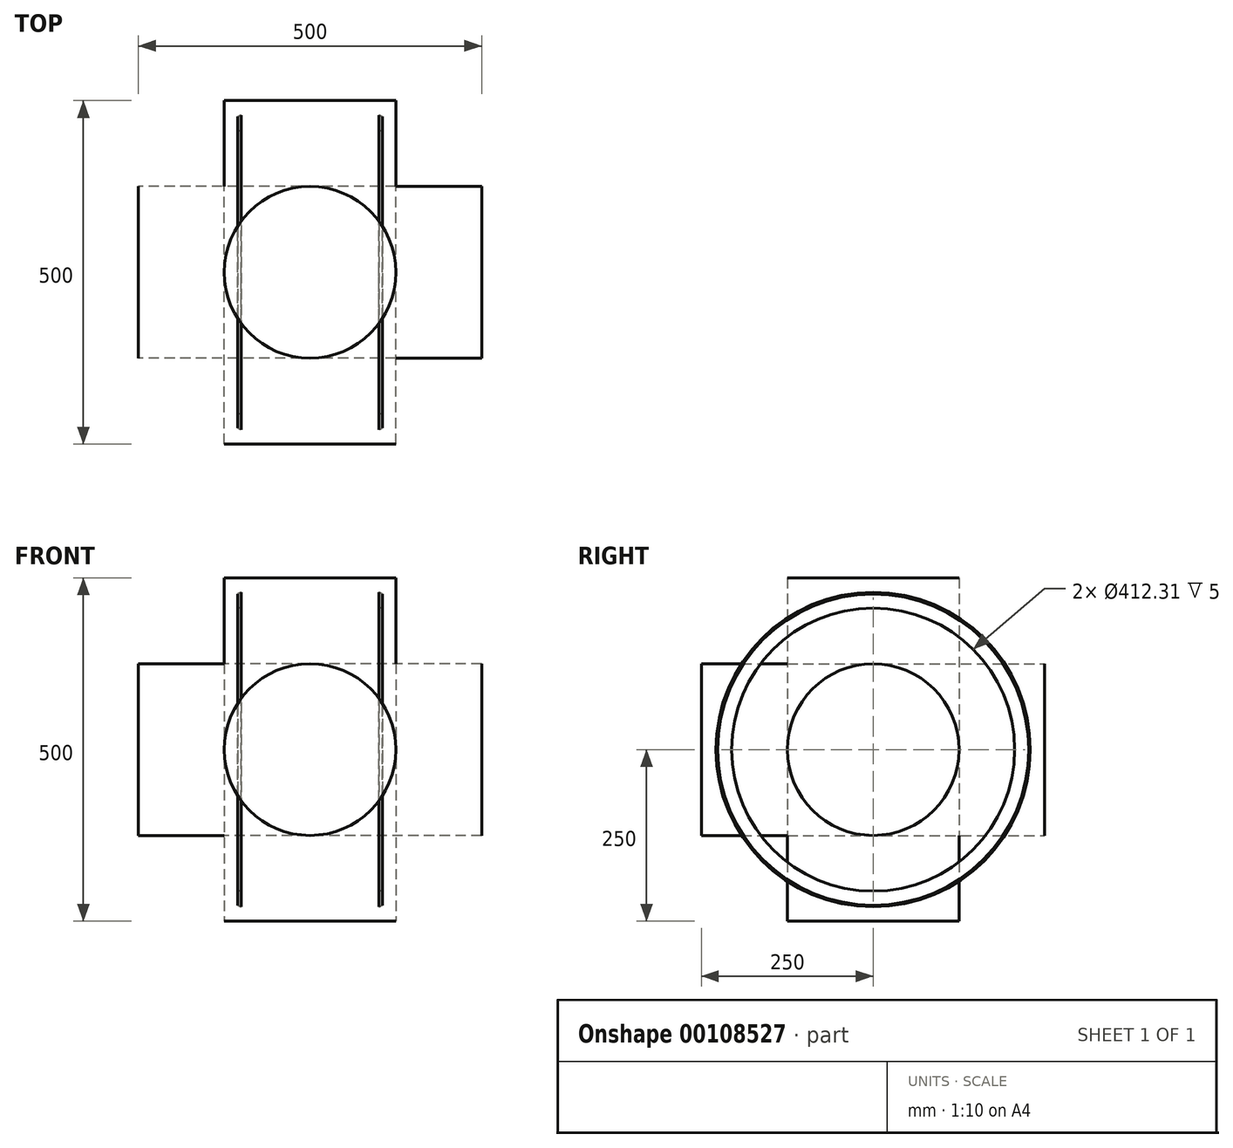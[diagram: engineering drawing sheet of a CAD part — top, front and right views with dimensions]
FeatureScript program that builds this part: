
annotation { "Feature Type Name" : "Feature", "Feature Type Description" : "" }
export const myFeature = defineFeature(function(context is Context, id is Id, definition is map)
    precondition{}
    {
        {
            var Q0;
            Q0=qCreatedBy(makeId("Top.planeOp"),FACE);
            var sketch = newSketch(context, id + "F0", { "sketchPlane" : qUnion([Q0])});
            skArc(sketch, "E0", {"start": v(-95, 225.83) * mm, "mid": v(0, 245) * mm, "end": v(95, 225.83) * mm});
            skArc(sketch, "E1", {"start": v(-100, 229.13) * mm, "mid": v(0, 250) * mm, "end": v(100, 229.13) * mm});
            skPoint(sketch, "E2", {"position": v(0, 250) * mm});
            skLineSegment(sketch, "E3", {"start": v(-100, 229.13) * mm, "end": v(-100, 206.15) * mm});
            skLineSegment(sketch, "E4", {"start": v(-100, 206.15) * mm, "end": v(-95, 206.15) * mm});
            skLineSegment(sketch, "E5", {"start": v(100, 229.13) * mm, "end": v(100, 206.15) * mm});
            skLineSegment(sketch, "E6", {"start": v(100, 206.15) * mm, "end": v(95, 206.15) * mm});
            skLineSegment(sketch, "E7", {"start": v(-49.24, 240) * mm, "end": v(49.24, 240) * mm});
            skPoint(sketch, "E8", {"position": v(0, 240) * mm});
            skLineSegment(sketch, "E9", {"start": v(-95, 0) * mm, "end": v(95, 0) * mm, "construction": true});
            skLineSegment(sketch, "E10", {"start": v(-95, 206.15) * mm, "end": v(-95, 0) * mm, "construction": true});
            skLineSegment(sketch, "E11", {"start": v(95, 206.15) * mm, "end": v(95, 225.83) * mm});
            skLineSegment(sketch, "E12", {"start": v(-95, 206.15) * mm, "end": v(-95, 225.83) * mm});
            skLineSegment(sketch, "E13", {"start": v(95, 0) * mm, "end": v(95, 206.15) * mm, "construction": true});
            skLineSegment(sketch, "E14.bottom", {"start": v(10, 245) * mm, "end": v(-10, 245) * mm});
            skLineSegment(sketch, "E14.top", {"start": v(10, 240) * mm, "end": v(-10, 240) * mm});
            skLineSegment(sketch, "E14.left", {"start": v(10, 245) * mm, "end": v(10, 240) * mm});
            skLineSegment(sketch, "E14.right", {"start": v(-10, 245) * mm, "end": v(-10, 240) * mm});
            skPoint(sketch, "E14.middle", {"position": v(0, 242.5) * mm});
            skLineSegment(sketch, "E15", {"start": v(95, 225) * mm, "end": v(85, 225) * mm});
            skLineSegment(sketch, "E16", {"start": v(85, 225) * mm, "end": v(85, 229.78) * mm});
            skLineSegment(sketch, "E17", {"start": v(-95, 225) * mm, "end": v(-85, 225) * mm});
            skLineSegment(sketch, "E18", {"start": v(-85, 225) * mm, "end": v(-85, 229.78) * mm});
            skLineSegment(sketch, "E19", {"start": v(-85, 225) * mm, "end": v(85, 225) * mm, "construction": true});
            skPoint(sketch, "E20.positionSnap0", {"position": v(0, 225) * mm});
            skLineSegment(sketch, "E21", {"start": v(-95, 225.83) * mm, "end": v(95, 225.83) * mm, "construction": true});
            skPoint(sketch, "E22", {"position": v(0, 225.83) * mm});
            skLineSegment(sketch, "E23", {"start": v(85, 225) * mm, "end": v(85, 220) * mm});
            skLineSegment(sketch, "E24", {"start": v(85, 220) * mm, "end": v(87.5, 220) * mm});
            skLineSegment(sketch, "E25", {"start": v(87.5, 220) * mm, "end": v(87.5, 225) * mm});
            skLineSegment(sketch, "E26", {"start": v(-85, 225) * mm, "end": v(-85, 220) * mm});
            skLineSegment(sketch, "E27", {"start": v(-85, 220) * mm, "end": v(-87.5, 220) * mm});
            skLineSegment(sketch, "E28", {"start": v(-87.5, 220) * mm, "end": v(-87.5, 225) * mm});
            skLineSegment(sketch, "E29", {"start": v(100.5, 0) * mm, "end": v(250, 0) * mm, "construction": true});
            skLineSegment(sketch, "E30", {"start": v(-100.5, 0) * mm, "end": v(-250, 0) * mm, "construction": true});
            skArc(sketch, "E31", {"start": v(100.5, 228.9) * mm, "mid": v(209.31, 136.7) * mm, "end": v(250, 0) * mm});
            skArc(sketch, "E32", {"start": v(-100.5, 228.9) * mm, "mid": v(-209.31, 136.7) * mm, "end": v(-250, 0) * mm});
            skArc(sketch, "E33", {"start": v(105.5, 215.57) * mm, "mid": v(203.62, 127.04) * mm, "end": v(240, 0) * mm});
            skArc(sketch, "E34", {"start": v(-105.5, 215.57) * mm, "mid": v(-203.62, 127.04) * mm, "end": v(-240, 0) * mm});
            skLineSegment(sketch, "E35", {"start": v(-250, 0) * mm, "end": v(-240, 0) * mm});
            skLineSegment(sketch, "E36", {"start": v(240, 0) * mm, "end": v(250, 0) * mm});
            skLineSegment(sketch, "E37", {"start": v(100.5, 206.15) * mm, "end": v(105.5, 206.15) * mm});
            skLineSegment(sketch, "E38", {"start": v(105.5, 206.15) * mm, "end": v(105.5, 215.57) * mm});
            skLineSegment(sketch, "E39", {"start": v(100.5, 228.9) * mm, "end": v(100.5, 206.15) * mm});
            skLineSegment(sketch, "E40", {"start": v(-100.5, 206.15) * mm, "end": v(-105.5, 206.15) * mm});
            skLineSegment(sketch, "E41", {"start": v(-105.5, 206.15) * mm, "end": v(-105.5, 215.57) * mm});
            skLineSegment(sketch, "E42", {"start": v(-100.5, 228.9) * mm, "end": v(-100.5, 206.15) * mm});
            skLineSegment(sketch, "E43", {"start": v(105.5, 215.57) * mm, "end": v(105.5, 226.65) * mm});
            skLineSegment(sketch, "E44", {"start": v(-105.5, 215.57) * mm, "end": v(-105.5, 226.65) * mm});
            skSolve(sketch);
        }
        {
            var Q0;
            Q0=qCreatedBy(makeId("Right.planeOp"),FACE);
            var sketch = newSketch(context, id + "F1", { "sketchPlane" : qUnion([Q0])});
            skCircle(sketch, "E45", {"center": v(0, 0) * mm, "radius": 125 * mm});
            skLineSegment(sketch, "E46", {"start": v(0, -77.8) * mm, "end": v(0, 75.57) * mm, "construction": true});
            skLineSegment(sketch, "E47", {"start": v(-74.6, 0) * mm, "end": v(71.66, 0) * mm, "construction": true});
            skCircle(sketch, "E48", {"center": v(0, 0) * mm, "radius": 150 * mm});
            skSolve(sketch);
        }
        {
            var Q0;
            Q0=qCreatedBy(makeId("Front.planeOp"),FACE);
            var sketch = newSketch(context, id + "F2", { "sketchPlane" : qUnion([Q0])});
            skCircle(sketch, "E49", {"center": v(0, 0) * mm, "radius": 125 * mm});
            skCircle(sketch, "E50", {"center": v(0, 0) * mm, "radius": 150 * mm});
            skSolve(sketch);
        }
        {
            var Q0;
            Q0=qCreatedBy(makeId("Top.planeOp"),FACE);
            var sketch = newSketch(context, id + "F3", { "sketchPlane" : qUnion([Q0])});
            skCircle(sketch, "E51", {"center": v(0, 0) * mm, "radius": 125 * mm});
            skCircle(sketch, "E52", {"center": v(0, 0) * mm, "radius": 150 * mm});
            skSolve(sketch);
        }
        {
            var Q0;
            Q0=makeQuery(id+"F0.imprint","IMPRINT",FACE,{"disambiguationData":[TD([[makeQuery(id+"F0.imprint","IMPRINT",EDGE,{"derivedFrom":sQuery(id+"F0.wireOp",EDGE,"E40")}),-1.0]])]});
            var Q1;
            Q1=makeQuery(id+"F0.imprint","IMPRINT",FACE,{"disambiguationData":[TD([[makeQuery(id+"F0.imprint","IMPRINT",EDGE,{"derivedFrom":sQuery(id+"F0.wireOp",EDGE,"E1")}),-1.0]])]});
            var Q2;
            Q2=makeQuery(id+"F0.imprint","IMPRINT",FACE,{"disambiguationData":[TD([[makeQuery(id+"F0.imprint","IMPRINT",EDGE,{"derivedFrom":sQuery(id+"F0.wireOp",EDGE,"E37")}),1.0]])]});
            var Q3;
            Q3=sQuery(id+"F0.wireOp",EDGE,"E9");
            revolve(context, id + "F4", {"entities" : qUnion([Q0, Q1, Q2]), "axis" : qUnion([Q3]), "revolveType" : RevolveType.FULL});
        }
        {
            var Q0;
            Q0=makeQuery(id+"F2.imprint","IMPRINT",FACE,{"disambiguationData":[TD([[makeQuery(id+"F2.imprint","IMPRINT",EDGE,{"derivedFrom":sQuery(id+"F2.wireOp",EDGE,"E49")}),1.0]])]});
            extrude(context, id + "F5", {"entities" : qUnion([Q0]), "endBound" : BoundingType.SYMMETRIC, "depth" : 500 * mm});
        }
        {
            var Q0;
            Q0=makeQuery(id+"F3.imprint","IMPRINT",FACE,{"disambiguationData":[TD([[makeQuery(id+"F3.imprint","IMPRINT",EDGE,{"derivedFrom":sQuery(id+"F3.wireOp",EDGE,"E51")}),1.0]])]});
            extrude(context, id + "F6", {"entities" : qUnion([Q0]), "endBound" : BoundingType.SYMMETRIC, "depth" : 500 * mm});
        }
        {
            var Q0;
            Q0=makeQuery(id+"F1.imprint","IMPRINT",FACE,{"disambiguationData":[TD([[makeQuery(id+"F1.imprint","IMPRINT",EDGE,{"derivedFrom":sQuery(id+"F1.wireOp",EDGE,"E45")}),1.0]])]});
            extrude(context, id + "F7", {"entities" : qUnion([Q0]), "endBound" : BoundingType.SYMMETRIC, "depth" : 500 * mm});
        }
    });
